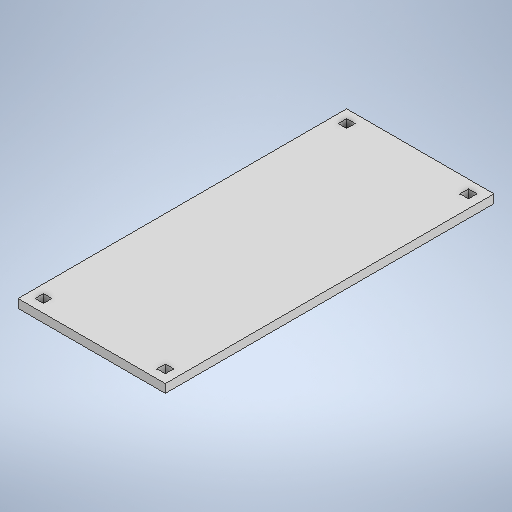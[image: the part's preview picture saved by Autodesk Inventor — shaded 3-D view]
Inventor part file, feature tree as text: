
AUTODESK INVENTOR PART (.ipt)
format: ipt  version: 2025 (Build 290162000, 162)  size: 259,072 bytes
history: native  units: in
note: dims shown in document units (in); Inventor stores cm internally (conversion verified against a paired STEP export)
features: extrude x2, sketch x2
ambient origin geometry x8: Origin, YZ Plane, XZ Plane, XY Plane, X Axis, Y Axis, Z Axis, Center Point
bodies: Solid1 (feature_tree)
feature tree (4):
  extrude  "Extrusion1"  Depth=20.4724in
  extrude  "Extrusion2"  Depth=1.1811in
  sketch  "Sketch1"  dims[d0=45.6693in d1=20.4724in]
  sketch  "Sketch2"  dims[d2=1.1811in d3=1.1811in d4=1.1811in d5=1.1811in d6=1.1811in d7=1.1811in d8=1.1811in d9=1.1811in d10=1.1811in d11=1.1811in d12=1.1811in d13=1.1811in d14=1.1811in d15=0.0in d16=25.5906in d17=11.811in d18=1.1811in d19=0.0in]
